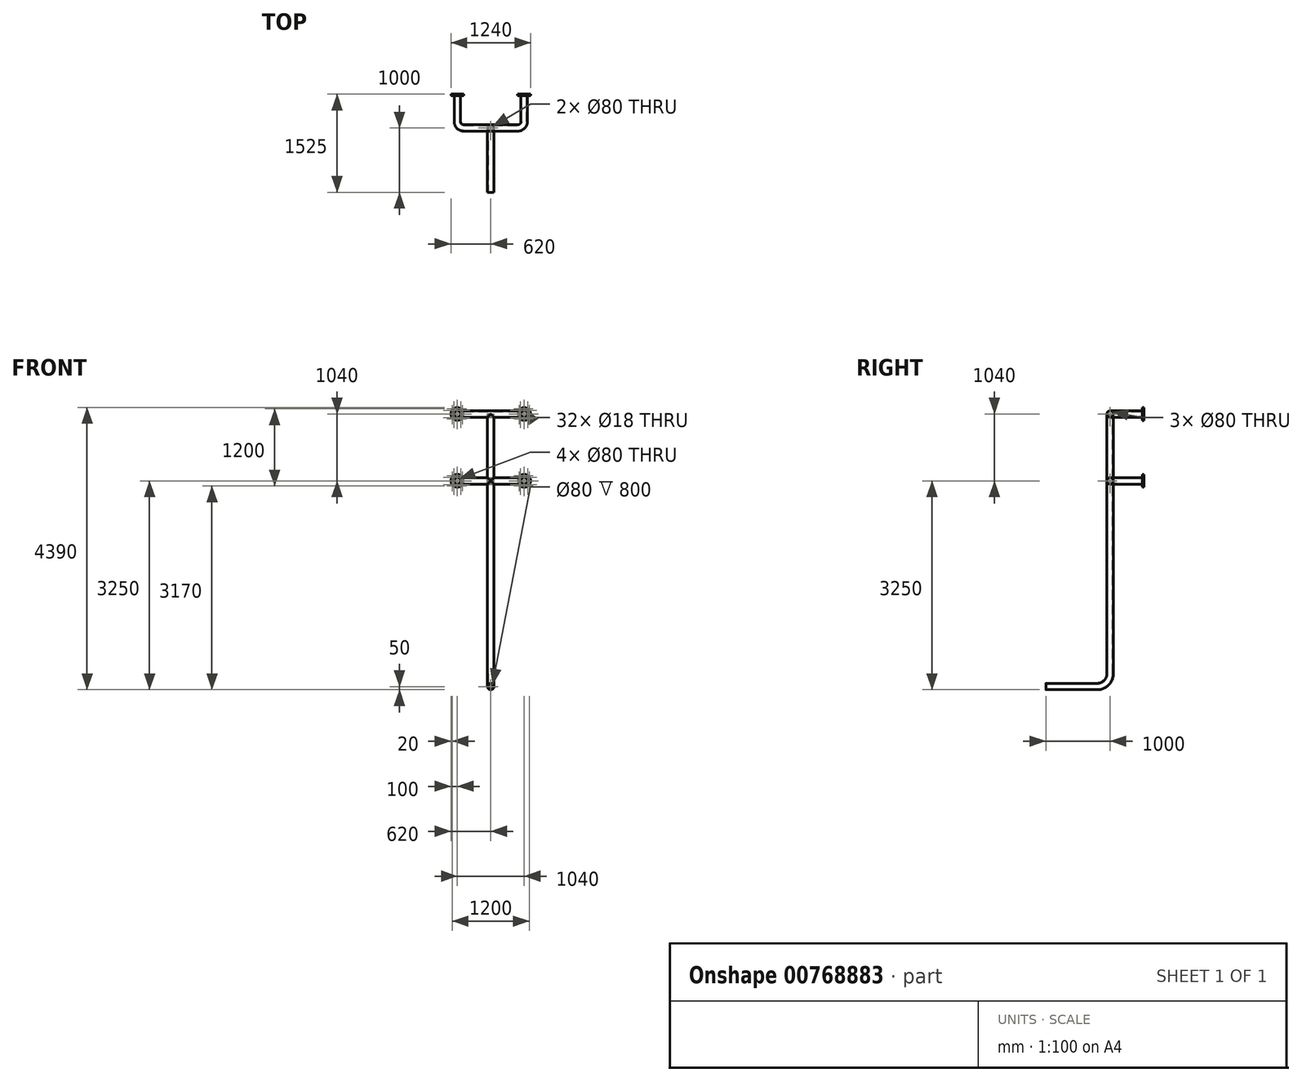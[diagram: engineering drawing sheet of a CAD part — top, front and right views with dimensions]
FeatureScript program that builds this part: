
annotation { "Feature Type Name" : "Feature", "Feature Type Description" : "" }
export const myFeature = defineFeature(function(context is Context, id is Id, definition is map)
    precondition{}
    {
        {
            var Q0;
            Q0=qCreatedBy(makeId("Front.planeOp"),FACE);
            var sketch = newSketch(context, id + "F0", { "sketchPlane" : qUnion([Q0])});
            skCircle(sketch, "E0", {"center": v(-520, 0) * mm, "radius": 40 * mm});
            skCircle(sketch, "E1", {"center": v(-520, 0) * mm, "radius": 100 * mm});
            skCircle(sketch, "E2", {"center": v(-520, 80) * mm, "radius": 9 * mm});
            skCircle(sketch, "E3.1.0", {"center": v(-576.57, 56.57) * mm, "radius": 9 * mm});
            skCircle(sketch, "E3.2.0", {"center": v(-600, 0) * mm, "radius": 9 * mm});
            skCircle(sketch, "E3.3.0", {"center": v(-576.57, -56.57) * mm, "radius": 9 * mm});
            skCircle(sketch, "E3.4.0", {"center": v(-520, -80) * mm, "radius": 9 * mm});
            skCircle(sketch, "E3.5.0", {"center": v(-463.43, -56.57) * mm, "radius": 9 * mm});
            skCircle(sketch, "E3.6.0", {"center": v(-440, 0) * mm, "radius": 9 * mm});
            skCircle(sketch, "E3.7.0", {"center": v(-463.43, 56.57) * mm, "radius": 9 * mm});
            skCircle(sketch, "E4.0.1.0", {"center": v(-520, 1040) * mm, "radius": 40 * mm});
            skCircle(sketch, "E4.0.1.1", {"center": v(-520, 1040) * mm, "radius": 100 * mm});
            skPoint(sketch, "E4.0.1.2", {"position": v(-520, 1040) * mm});
            skCircle(sketch, "E4.0.1.3", {"center": v(-576.57, 1096.57) * mm, "radius": 9 * mm});
            skCircle(sketch, "E4.0.1.4", {"center": v(-600, 1040) * mm, "radius": 9 * mm});
            skCircle(sketch, "E4.0.1.5", {"center": v(-576.57, 983.43) * mm, "radius": 9 * mm});
            skCircle(sketch, "E4.0.1.6", {"center": v(-520, 960) * mm, "radius": 9 * mm});
            skCircle(sketch, "E4.0.1.7", {"center": v(-463.43, 983.43) * mm, "radius": 9 * mm});
            skCircle(sketch, "E4.0.1.8", {"center": v(-440, 1040) * mm, "radius": 9 * mm});
            skCircle(sketch, "E4.0.1.9", {"center": v(-463.43, 1096.57) * mm, "radius": 9 * mm});
            skCircle(sketch, "E4.0.1.10", {"center": v(-520, 1120) * mm, "radius": 9 * mm});
            skCircle(sketch, "E4.1.0.0", {"center": v(520, 0) * mm, "radius": 40 * mm});
            skCircle(sketch, "E4.1.0.1", {"center": v(520, 0) * mm, "radius": 100 * mm});
            skPoint(sketch, "E4.1.0.2", {"position": v(520, 0) * mm});
            skCircle(sketch, "E4.1.0.3", {"center": v(463.43, 56.57) * mm, "radius": 9 * mm});
            skCircle(sketch, "E4.1.0.4", {"center": v(440, 0) * mm, "radius": 9 * mm});
            skCircle(sketch, "E4.1.0.5", {"center": v(463.43, -56.57) * mm, "radius": 9 * mm});
            skCircle(sketch, "E4.1.0.6", {"center": v(520, -80) * mm, "radius": 9 * mm});
            skCircle(sketch, "E4.1.0.7", {"center": v(576.57, -56.57) * mm, "radius": 9 * mm});
            skCircle(sketch, "E4.1.0.8", {"center": v(600, 0) * mm, "radius": 9 * mm});
            skCircle(sketch, "E4.1.0.9", {"center": v(576.57, 56.57) * mm, "radius": 9 * mm});
            skCircle(sketch, "E4.1.0.10", {"center": v(520, 80) * mm, "radius": 9 * mm});
            skCircle(sketch, "E4.1.1.0", {"center": v(520, 1040) * mm, "radius": 40 * mm});
            skCircle(sketch, "E4.1.1.1", {"center": v(520, 1040) * mm, "radius": 100 * mm});
            skPoint(sketch, "E4.1.1.2", {"position": v(520, 1040) * mm});
            skCircle(sketch, "E4.1.1.3", {"center": v(463.43, 1096.57) * mm, "radius": 9 * mm});
            skCircle(sketch, "E4.1.1.4", {"center": v(440, 1040) * mm, "radius": 9 * mm});
            skCircle(sketch, "E4.1.1.5", {"center": v(463.43, 983.43) * mm, "radius": 9 * mm});
            skCircle(sketch, "E4.1.1.6", {"center": v(520, 960) * mm, "radius": 9 * mm});
            skCircle(sketch, "E4.1.1.7", {"center": v(576.57, 983.43) * mm, "radius": 9 * mm});
            skCircle(sketch, "E4.1.1.8", {"center": v(600, 1040) * mm, "radius": 9 * mm});
            skCircle(sketch, "E4.1.1.9", {"center": v(576.57, 1096.57) * mm, "radius": 9 * mm});
            skCircle(sketch, "E4.1.1.10", {"center": v(520, 1120) * mm, "radius": 9 * mm});
            skLineSegment(sketch, "E4.direction1", {"start": v(-576.57, -56.57) * mm, "end": v(463.43, -56.57) * mm, "construction": true});
            skLineSegment(sketch, "E4.direction2", {"start": v(-576.57, -56.57) * mm, "end": v(-576.57, 983.43) * mm, "construction": true});
            skSolve(sketch);
        }
        {
            var Q0;
            Q0 = qSketchRegion(id + "F0", true);
            extrude(context, id + "F1", {"entities" : qUnion([Q0]), "depth" : 25 * mm, "offsetDistance" : 25 * mm});
        }
        {
            var Q0;
            Q0=makeQuery(id+"F1.opExtrude","CAP_FACE",FACE,{"disambiguationData":[OSD([sQuery(id+"F0.wireOp",EDGE,"E0"),sQuery(id+"F0.wireOp",EDGE,"E1"),sQuery(id+"F0.wireOp",EDGE,"E2"),sQuery(id+"F0.wireOp",EDGE,"E3.1.0"),sQuery(id+"F0.wireOp",EDGE,"E3.2.0"),sQuery(id+"F0.wireOp",EDGE,"E3.3.0"),sQuery(id+"F0.wireOp",EDGE,"E3.4.0"),sQuery(id+"F0.wireOp",EDGE,"E3.5.0"),sQuery(id+"F0.wireOp",EDGE,"E3.6.0"),sQuery(id+"F0.wireOp",EDGE,"E3.7.0")])],"isStart":false});
            var sketch = newSketch(context, id + "F2", { "sketchPlane" : qUnion([Q0])});
            skCircle(sketch, "E5", {"center": v(-520, 0) * mm, "radius": 50 * mm});
            skCircle(sketch, "E6.0.1.0", {"center": v(-520, 1040) * mm, "radius": 50 * mm});
            skCircle(sketch, "E6.1.0.0", {"center": v(520, 0) * mm, "radius": 50 * mm});
            skCircle(sketch, "E6.1.1.0", {"center": v(520, 1040) * mm, "radius": 50 * mm});
            skLineSegment(sketch, "E6.direction1", {"start": v(-520, 0) * mm, "end": v(520, 0) * mm, "construction": true});
            skLineSegment(sketch, "E6.direction2", {"start": v(-520, 0) * mm, "end": v(-520, 1040) * mm, "construction": true});
            skCircle(sketch, "E7", {"center": v(-520, 0) * mm, "radius": 40 * mm});
            skCircle(sketch, "E8.0.1.0", {"center": v(-520, 1040) * mm, "radius": 40 * mm});
            skCircle(sketch, "E8.1.0.0", {"center": v(520, 0) * mm, "radius": 40 * mm});
            skCircle(sketch, "E8.1.1.0", {"center": v(520, 1040) * mm, "radius": 40 * mm});
            skSolve(sketch);
        }
        {
            var Q0;
            Q0=qCreatedBy(makeId("Top.planeOp"),FACE);
            var sketch = newSketch(context, id + "F3", { "sketchPlane" : qUnion([Q0])});
            skPoint(sketch, "E9.0", {"position": v(-520, -25) * mm});
            skPoint(sketch, "E10.0", {"position": v(520, -25) * mm});
            skLineSegment(sketch, "E11", {"start": v(-520, -25) * mm, "end": v(-520, -425) * mm});
            skLineSegment(sketch, "E12", {"start": v(-420, -525) * mm, "end": v(420, -525) * mm});
            skLineSegment(sketch, "E13", {"start": v(520, -425) * mm, "end": v(520, -25) * mm});
            skPoint(sketch, "E14.visualSharp", {"position": v(-520, -525) * mm});
            skArc(sketch, "E14.filletArc", {"start": v(-520, -425) * mm, "mid": v(-490.71, -495.71) * mm, "end": v(-420, -525) * mm});
            skPoint(sketch, "E15.visualSharp", {"position": v(520, -525) * mm});
            skArc(sketch, "E15.filletArc", {"start": v(420, -525) * mm, "mid": v(490.71, -495.71) * mm, "end": v(520, -425) * mm});
            skSolve(sketch);
        }
        {
            var Q0;
            Q0=qCreatedBy(makeId("Top.planeOp"),FACE);
            cPlane(context, id + "F4", {"entities" : qUnion([Q0]), "cplaneType" : CPlaneType.OFFSET, "offset" : 1040 * mm, "width" : 150 * mm, "height" : 150 * mm});
        }
        {
            var Q0;
            Q0=qCreatedBy(id+"F4.planeOp",FACE);
            var sketch = newSketch(context, id + "F5", { "sketchPlane" : qUnion([Q0])});
            skPoint(sketch, "E16.0", {"position": v(-520, -25) * mm});
            skPoint(sketch, "E17.0", {"position": v(520, -25) * mm});
            skLineSegment(sketch, "E18", {"start": v(-520, -25) * mm, "end": v(-520, -425) * mm});
            skLineSegment(sketch, "E19", {"start": v(-420, -525) * mm, "end": v(420, -525) * mm});
            skLineSegment(sketch, "E20", {"start": v(520, -425) * mm, "end": v(520, -25) * mm});
            skPoint(sketch, "E21.visualSharp", {"position": v(-520, -525) * mm});
            skArc(sketch, "E21.filletArc", {"start": v(-520, -425) * mm, "mid": v(-490.71, -495.71) * mm, "end": v(-420, -525) * mm});
            skPoint(sketch, "E22.visualSharp", {"position": v(520, -525) * mm});
            skArc(sketch, "E22.filletArc", {"start": v(420, -525) * mm, "mid": v(490.71, -495.71) * mm, "end": v(520, -425) * mm});
            skSolve(sketch);
        }
        {
            var Q0;
            Q0=qCreatedBy(makeId("Front.planeOp"),FACE);
            cPlane(context, id + "F6", {"entities" : qUnion([Q0]), "cplaneType" : CPlaneType.OFFSET, "offset" : 525 * mm, "width" : 150 * mm, "height" : 150 * mm});
        }
        {
            var Q0;
            Q0=qCreatedBy(id+"F6.planeOp",FACE);
            var sketch = newSketch(context, id + "F7", { "sketchPlane" : qUnion([Q0])});
            skLineSegment(sketch, "E23.0", {"start": v(-420, 1040) * mm, "end": v(420, 1040) * mm});
            skLineSegment(sketch, "E24.0", {"start": v(-420, 0) * mm, "end": v(420, 0) * mm});
            skLineSegment(sketch, "E25", {"start": v(0, 1040) * mm, "end": v(0, 0) * mm});
            skLineSegment(sketch, "E26", {"start": v(0, 0) * mm, "end": v(0, -200) * mm});
            skLineSegment(sketch, "E27", {"start": v(0, -200) * mm, "end": v(0, -3200) * mm});
            skSolve(sketch);
        }
        {
            var Q0;
            Q0=makeQuery(id+"F2.imprint","IMPRINT",FACE,{"disambiguationData":[TD([[makeQuery(id+"F2.imprint","IMPRINT",EDGE,{"derivedFrom":sQuery(id+"F2.wireOp",EDGE,"E6.0.1.0")}),1.0]])]});
            var Q1;
            Q1=sQuery(id+"F5.wireOp",EDGE,"E18");
            var Q2;
            Q2=sQuery(id+"F5.wireOp",EDGE,"E21.filletArc");
            var Q3;
            Q3=sQuery(id+"F7.wireOp",EDGE,"E23.0");
            var Q4;
            Q4=sQuery(id+"F5.wireOp",EDGE,"E22.filletArc");
            var Q5;
            Q5=sQuery(id+"F5.wireOp",EDGE,"E20");
            sweep(context, id + "F8", {"operationType" : NewBodyOperationType.ADD, "profiles" : qUnion([Q0]), "path" : qUnion([Q1, Q2, Q3, Q4, Q5])});
        }
        {
            var Q0;
            Q0=makeQuery(id+"F2.imprint","IMPRINT",FACE,{"disambiguationData":[TD([[makeQuery(id+"F2.imprint","IMPRINT",EDGE,{"derivedFrom":sQuery(id+"F2.wireOp",EDGE,"E5")}),1.0]])]});
            var Q1;
            Q1=sQuery(id+"F3.wireOp",EDGE,"E11");
            var Q2;
            Q2=sQuery(id+"F3.wireOp",EDGE,"E14.filletArc");
            var Q3;
            Q3=sQuery(id+"F3.wireOp",EDGE,"E12");
            var Q4;
            Q4=sQuery(id+"F3.wireOp",EDGE,"E15.filletArc");
            var Q5;
            Q5=sQuery(id+"F3.wireOp",EDGE,"E13");
            sweep(context, id + "F9", {"operationType" : NewBodyOperationType.ADD, "profiles" : qUnion([Q0]), "path" : qUnion([Q1, Q2, Q3, Q4, Q5])});
        }
        {
            var Q0;
            Q0=qCreatedBy(makeId("Top.planeOp"),FACE);
            cPlane(context, id + "F10", {"entities" : qUnion([Q0]), "cplaneType" : CPlaneType.OFFSET, "offset" : 200 * mm, "oppositeDirection" : true, "width" : 150 * mm, "height" : 150 * mm});
        }
        {
            var Q0;
            Q0=qCreatedBy(id+"F10.planeOp",FACE);
            var sketch = newSketch(context, id + "F11", { "sketchPlane" : qUnion([Q0])});
            skCircle(sketch, "E28", {"center": v(0, -525) * mm, "radius": 50 * mm});
            skCircle(sketch, "E29", {"center": v(0, -525) * mm, "radius": 40 * mm});
            skSolve(sketch);
        }
        {
            var Q0;
            Q0=makeQuery(id+"F11.imprint","IMPRINT",FACE,{"disambiguationData":[TD([[makeQuery(id+"F11.imprint","IMPRINT",EDGE,{"derivedFrom":sQuery(id+"F11.wireOp",EDGE,"E28")}),1.0]])]});
            var Q1;
            Q1=sQuery(id+"F7.wireOp",EDGE,"E26");
            var Q2;
            Q2=sQuery(id+"F7.wireOp",EDGE,"E25");
            sweep(context, id + "F12", {"operationType" : NewBodyOperationType.ADD, "profiles" : qUnion([Q0]), "path" : qUnion([Q1, Q2])});
        }
        {
            var Q0;
            Q0=qCreatedBy(makeId("Right.planeOp"),FACE);
            var sketch = newSketch(context, id + "F13", { "sketchPlane" : qUnion([Q0])});
            skLineSegment(sketch, "E30.0", {"start": v(-525, -200) * mm, "end": v(-525, -3000) * mm});
            skLineSegment(sketch, "E31", {"start": v(-725, -3200) * mm, "end": v(-1525, -3200) * mm});
            skPoint(sketch, "E32.visualSharp", {"position": v(-525, -3200) * mm});
            skArc(sketch, "E32.filletArc", {"start": v(-725, -3200) * mm, "mid": v(-583.58, -3141.42) * mm, "end": v(-525, -3000) * mm});
            skSolve(sketch);
        }
        {
            var Q0;
            Q0=makeQuery(id+"F12.opSweep","CAP_FACE",FACE,{"disambiguationData":[OSD([sQuery(id+"F7.wireOp",VERTEX,"E26.end"),sQuery(id+"F11.wireOp",EDGE,"E28"),sQuery(id+"F11.wireOp",EDGE,"E29")])],"isStart":true});
            var Q1;
            Q1=sQuery(id+"F13.wireOp",EDGE,"E30.0");
            var Q2;
            Q2=sQuery(id+"F13.wireOp",EDGE,"E32.filletArc");
            var Q3;
            Q3=sQuery(id+"F13.wireOp",EDGE,"E31");
            sweep(context, id + "F14", {"operationType" : NewBodyOperationType.ADD, "profiles" : qUnion([Q0]), "path" : qUnion([Q1, Q2, Q3])});
        }
    });
